# Revit family: Mailboxes_4C-Salsbury_Industries-Pedestal_Mounted-11_Door_High_Units
name_source: partatom
category: Specialty Equipment
revit_build: Autodesk Revit 2016 (Build: 20190507_1515(x64)
units: mm (PartAtom-declared; Revit-internal decimal feet)

## family parameters
Always vertical = Yes
Cut with Voids When Loaded = No
OmniClass Number = 23.40.90.14.11
OmniClass Title = Mail Boxes
Part Type = Normal
Room Calculation Point = No
Round Connector Dimension = Use Diameter
Shared = No
Work Plane-Based = No

## types (7) — shared parameters
4C Unit Elevation = 26.375 "
4C Unit Height = 41 "
Assembly Code = C1030910
Assembly Description = Mailboxes
Depth = 19 "
Height = 69.125 "
Lock Material = Stainless Steel - Salsbury Finish -  Polished
Manufacturer = Salsbury Industries
MasterFormat Number = 10 55 00
MasterFormat Title = Postal Specialties
OmniClass 23 Number = 23.40.90.14.11
OmniClass 23 Title = Mail Boxes
Pedestal Height = 26 "
Type Comments = Pedestal Mounted 4C Horizontal Mailboxes - Front Loading
URL = www.mailboxes.com
Version = 3.0 (01/30/20)
Vertical Center Divider = Yes

## per-type parameters (varying)
| type | 4C Unit | Description | Width |
| 3411D-20 | Mailboxes_4C-Salsbury_Industries-Front_Load-11_Door_High_Units : 3711D-20 FL | 11 Door High Unit:  20 MB1, OM2 | 32.25 " |
| 3411D-15 | Mailboxes_4C-Salsbury_Industries-Front_Load-11_Door_High_Units : 3711D-15 FL | 11 Door High Unit:  15 MB1, 1 PL5, OM2 | 32.25 " |
| 3411D-10 | Mailboxes_4C-Salsbury_Industries-Front_Load-11_Door_High_Units : 3711D-10 FL | 11 Door High Unit:  10 MB1, 2 PL5, OM2 | 32.25 " |
| 3411D-4P | Mailboxes_4C-Salsbury_Industries-Front_Load-11_Door_High_Units : 3711D-4P FL | 11 Door High Unit:  3 PL5, 1 PL6, CA | 32.25 " |
| 3411S-04 | Mailboxes_4C-Salsbury_Industries-Front_Load-11_Door_High_Units : 3711S-04 FL | 11 Door High Unit:  4 MB1, 1 PL5, OM2 | 17.496 " |
| 3411S-2P | Mailboxes_4C-Salsbury_Industries-Front_Load-11_Door_High_Units : 3711S-2P FL | 11 Door High Unit:  1 PL5, 1 PL6 | 17.496 " |
| 3411S-09 | Mailboxes_4C-Salsbury_Industries-Front_Load-11_Door_High_Units : 3711S-09 FL | 11 Door High Unit:  9 MB1, OM2 | 17.496 " |

note: column(s) folded — value = type name in every type: Model

## geometry (parser evidence)
native form markers: Extrusion x4, Sweep x16
no freeform markers — native parametric forms only
